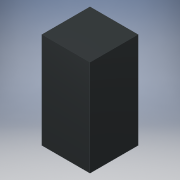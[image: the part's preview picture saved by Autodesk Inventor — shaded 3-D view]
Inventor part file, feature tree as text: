
AUTODESK INVENTOR PART (.ipt)
format: ipt  version: 2019 (Build 230136000, 136)  size: 96,768 bytes
history: native  units: in
note: dims shown in document units (in); Inventor stores cm internally (conversion verified against a paired STEP export)
features: extrude x2, sketch x2
ambient origin geometry x8: Origin, YZ Plane, XZ Plane, XY Plane, X Axis, Y Axis, Z Axis, Center Point
bodies: Solid1 (feature_tree)
feature tree (4):
  extrude  "Extrusion1"  Depth=4.0in
  extrude  "Extrusion2"  Depth=1.0in TaperAngle=0.0deg
  sketch  "Sketch1"  dims[d0=2.0in d1=4.0in]
  sketch  "Sketch2"  dims[d2=2.0in d3=0.0in d4=1.0in d5=0.0in]
